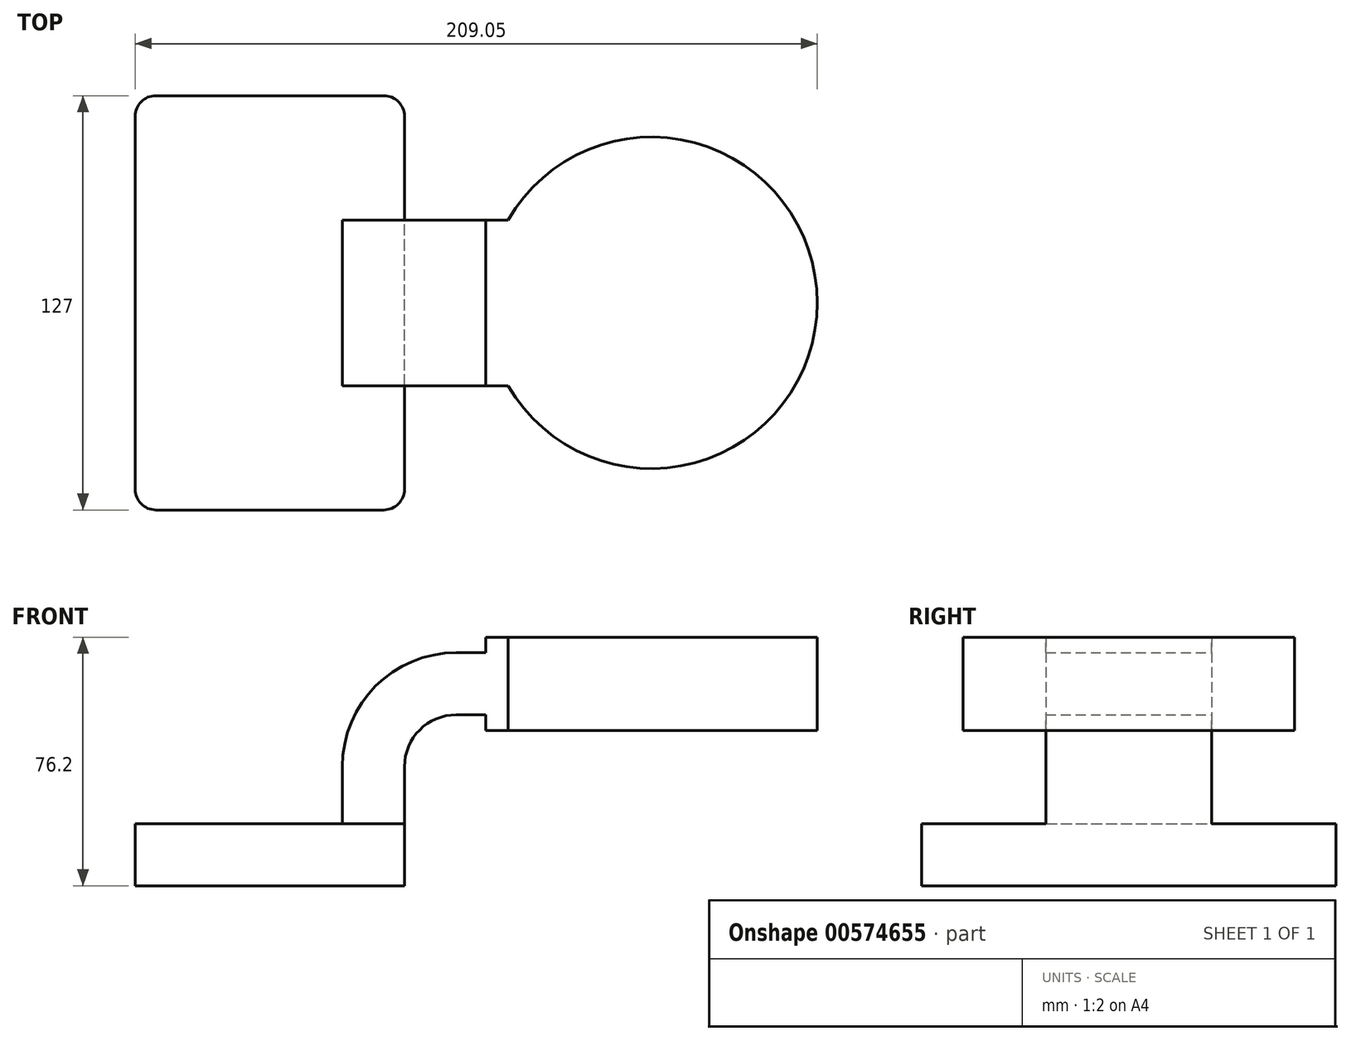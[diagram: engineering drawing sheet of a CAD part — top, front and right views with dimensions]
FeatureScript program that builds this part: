
annotation { "Feature Type Name" : "Feature", "Feature Type Description" : "" }
export const myFeature = defineFeature(function(context is Context, id is Id, definition is map)
    precondition{}
    {
        {
            var Q0;
            Q0=qCreatedBy(makeId("Front.planeOp"),FACE);
            var sketch = newSketch(context, id + "F0", { "sketchPlane" : qUnion([Q0])});
            skLineSegment(sketch, "E0.bottom", {"start": v(41.27, 9.53) * mm, "end": v(-41.28, 9.53) * mm});
            skLineSegment(sketch, "E0.top", {"start": v(41.28, -9.52) * mm, "end": v(-41.27, -9.52) * mm});
            skLineSegment(sketch, "E0.left", {"start": v(41.28, 9.53) * mm, "end": v(41.28, -9.52) * mm});
            skLineSegment(sketch, "E0.right", {"start": v(-41.28, 9.53) * mm, "end": v(-41.27, -9.52) * mm});
            skPoint(sketch, "E0.middle", {"position": v(0, 0) * mm});
            skLineSegment(sketch, "E1.bottom", {"start": v(66.18, 38.1) * mm, "end": v(116.98, 38.1) * mm});
            skLineSegment(sketch, "E1.top", {"start": v(66.18, 66.68) * mm, "end": v(116.98, 66.68) * mm});
            skLineSegment(sketch, "E1.left", {"start": v(66.18, 38.1) * mm, "end": v(66.18, 66.68) * mm});
            skLineSegment(sketch, "E1.right", {"start": v(116.98, 38.1) * mm, "end": v(116.98, 66.68) * mm});
            skPoint(sketch, "E1.middle", {"position": v(91.58, 52.39) * mm});
            skLineSegment(sketch, "E2", {"start": v(41.27, 9.53) * mm, "end": v(41.27, 27) * mm});
            skArc(sketch, "E3", {"start": v(41.27, 27) * mm, "mid": v(45.92, 38.23) * mm, "end": v(57.15, 42.88) * mm});
            skLineSegment(sketch, "E4", {"start": v(57.15, 42.88) * mm, "end": v(85.72, 42.88) * mm});
            skLineSegment(sketch, "E5.0", {"start": v(57.15, 61.93) * mm, "end": v(85.72, 61.93) * mm});
            skArc(sketch, "E5.1", {"start": v(22.23, 27) * mm, "mid": v(32.45, 51.7) * mm, "end": v(57.15, 61.93) * mm});
            skLineSegment(sketch, "E5.2", {"start": v(22.22, 9.53) * mm, "end": v(22.22, 27) * mm});
            skFitSpline(sketch, "E6", {"points": [v(-41.28, 9.52) * mm, v(57.15, 61.93) * mm], "startDerivative": vector(-1.05, 122.3) * mm, "endDerivative": vector(149.53, -0.77) * mm});
            skSolve(sketch);
        }
        {
            var Q0;
            Q0=makeQuery(id+"F0.imprint","IMPRINT",FACE,{"disambiguationData":[TD([[makeQuery(id+"F0.imprint","IMPRINT",EDGE,{"derivedFrom":sQuery(id+"F0.wireOp",EDGE,"E0.top")}),-1.0]])]});
            extrude(context, id + "F1", {"entities" : qUnion([Q0]), "endBound" : BoundingType.SYMMETRIC, "depth" : 127 * mm, "offsetDistance" : 25.4 * mm});
        }
        {
            var Q0;
            {var subQ1=sQuery(id+"F0.wireOp",EDGE,"E2");Q0=makeQuery(id+"F0.imprint","IMPRINT",FACE,{"disambiguationData":[TD([[makeQuery(id+"F0.imprint","IMPRINT",EDGE,{"derivedFrom":subQ1}),1.0]])]});}
            var Q1;
            {var subQ3=sQuery(id+"F0.wireOp",EDGE,"E1.bottom");Q1=makeQuery(id+"F0.imprint","IMPRINT",FACE,{"disambiguationData":[TD([[makeQuery(id+"F0.imprint","IMPRINT",EDGE,{"derivedFrom":subQ3}),1.0]])]});}
            extrude(context, id + "F2", {"entities" : qUnion([Q0, Q1]), "operationType" : NewBodyOperationType.ADD, "endBound" : BoundingType.SYMMETRIC, "depth" : 50.8 * mm, "offsetDistance" : 25.4 * mm});
        }
        {
            var Q0;
            Q0=makeQuery(id+"F0.imprint","IMPRINT",FACE,{"disambiguationData":[TD([[makeQuery(id+"F0.imprint","IMPRINT",EDGE,{"derivedFrom":sQuery(id+"F0.wireOp",EDGE,"E5.1")}),1.0]])]});
            extrude(context, id + "F3", {"entities" : qUnion([Q0]), "operationType" : NewBodyOperationType.ADD, "endBound" : BoundingType.SYMMETRIC, "depth" : 15.88 * mm, "offsetDistance" : 25.4 * mm});
        }
        {
            var Q0;
            {var subQ3=sQuery(id+"F0.wireOp",EDGE,"E1.bottom");Q0=makeQuery(id+"F0.imprint","IMPRINT",FACE,{"disambiguationData":[TD([[makeQuery(id+"F0.imprint","IMPRINT",EDGE,{"derivedFrom":subQ3}),1.0]])]});}
            var Q1;
            Q1=sQuery(id+"F0.wireOp",EDGE,"E1.right");
            revolve(context, id + "F4", {"operationType" : NewBodyOperationType.ADD, "entities" : qUnion([Q0]), "axis" : qUnion([Q1]), "revolveType" : RevolveType.FULL});
        }
        {
            var Q0;
            Q0=makeQuery(id+"F1.opExtrude","CAP_EDGE",EDGE,{"disambiguationData":[OSD([sQuery(id+"F0.wireOp",EDGE,"E0.left")])],"isStart":true});
            var Q1;
            Q1=makeQuery(id+"F1.opExtrude","CAP_EDGE",EDGE,{"disambiguationData":[OSD([sQuery(id+"F0.wireOp",EDGE,"E0.left")])],"isStart":false});
            var Q2;
            Q2=makeQuery(id+"F1.opExtrude","CAP_EDGE",EDGE,{"disambiguationData":[OSD([sQuery(id+"F0.wireOp",EDGE,"E0.right")])],"isStart":false});
            var Q3;
            Q3=makeQuery(id+"F1.opExtrude","CAP_EDGE",EDGE,{"disambiguationData":[OSD([sQuery(id+"F0.wireOp",EDGE,"E0.right")])],"isStart":true});
            fillet(context, id + "F5", {"entities" : qUnion([Q0, Q1, Q2, Q3]), "radius" : 6.35 * mm, "tangentPropagation" : true, "allowEdgeOverflow" : false});
        }
    });
